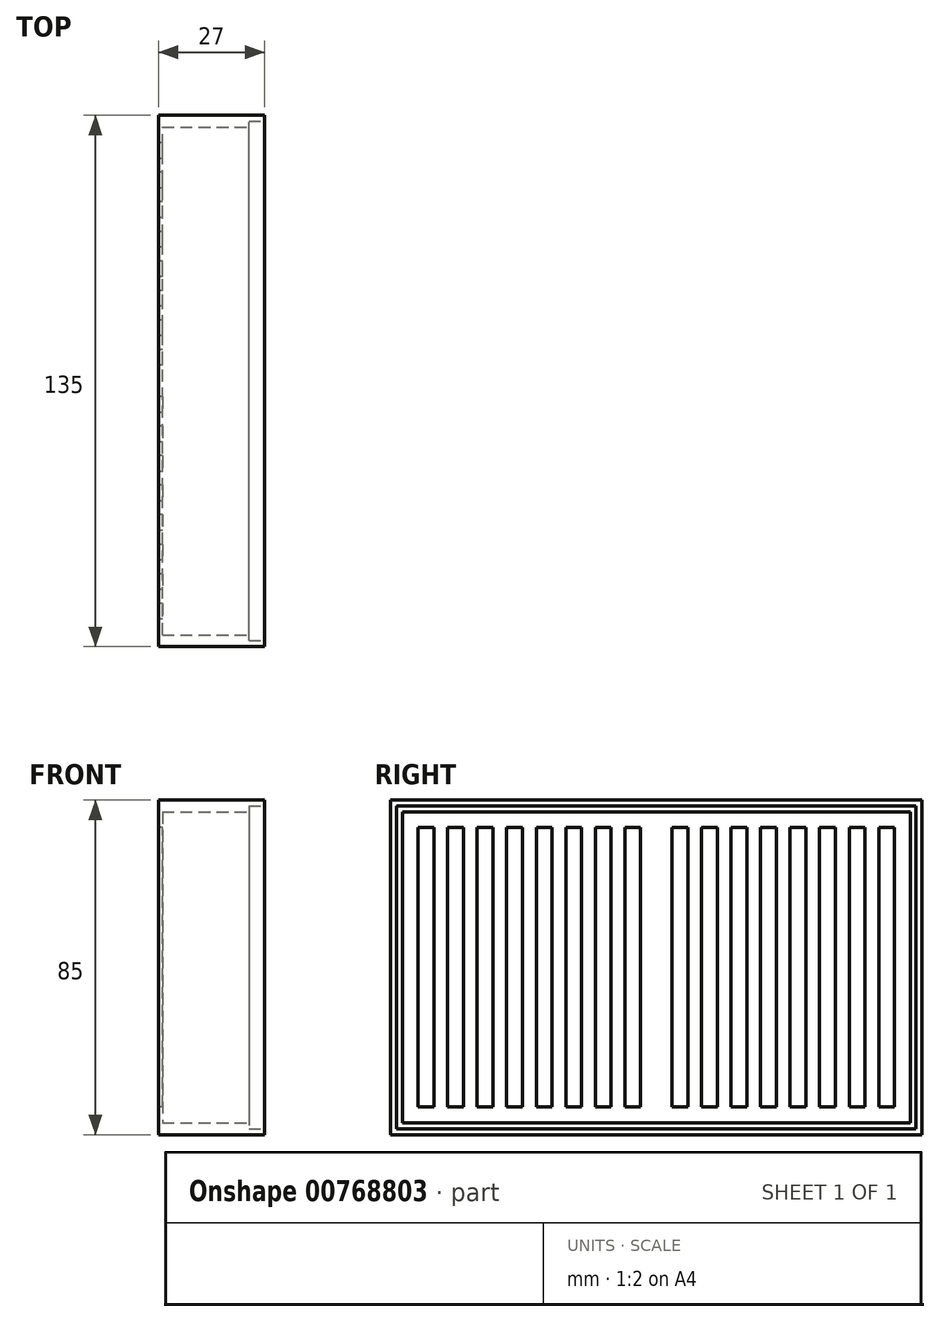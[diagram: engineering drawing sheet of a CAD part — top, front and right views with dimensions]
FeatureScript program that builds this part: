
annotation { "Feature Type Name" : "Feature", "Feature Type Description" : "" }
export const myFeature = defineFeature(function(context is Context, id is Id, definition is map)
    precondition{}
    {
        {
            var Q0;
            Q0=qCreatedBy(makeId("Right.planeOp"),FACE);
            var sketch = newSketch(context, id + "F0", { "sketchPlane" : qUnion([Q0])});
            skLineSegment(sketch, "E0.bottom", {"start": v(-67.5, 42.5) * mm, "end": v(67.5, 42.5) * mm});
            skLineSegment(sketch, "E0.top", {"start": v(-67.5, -42.5) * mm, "end": v(67.5, -42.5) * mm});
            skLineSegment(sketch, "E0.left", {"start": v(-67.5, 42.5) * mm, "end": v(-67.5, -42.5) * mm});
            skLineSegment(sketch, "E0.right", {"start": v(67.5, 42.5) * mm, "end": v(67.5, -42.5) * mm});
            skPoint(sketch, "E1", {"position": v(0, 42.5) * mm});
            skPoint(sketch, "E2", {"position": v(-67.5, 0) * mm});
            skSolve(sketch);
        }
        {
            var Q0;
            Q0 = qSketchRegion(id + "F0", true);
            extrude(context, id + "F1", {"entities" : qUnion([Q0]), "endBound" : BoundingType.SYMMETRIC, "depth" : 28 * mm, "offsetDistance" : 25 * mm});
        }
        {
            var Q0;
            Q0=makeQuery(id+"F1.opExtrude","CAP_FACE",FACE,{"disambiguationData":[OSD([sQuery(id+"F0.wireOp",EDGE,"E0.bottom"),sQuery(id+"F0.wireOp",EDGE,"E0.top"),sQuery(id+"F0.wireOp",EDGE,"E0.left"),sQuery(id+"F0.wireOp",EDGE,"E0.right")])],"isStart":false});
            var sketch = newSketch(context, id + "F2", { "sketchPlane" : qUnion([Q0])});
            skLineSegment(sketch, "E3.bottom", {"start": v(-64.5, 39.5) * mm, "end": v(64.5, 39.5) * mm});
            skLineSegment(sketch, "E3.top", {"start": v(-64.5, -39.5) * mm, "end": v(64.5, -39.5) * mm});
            skLineSegment(sketch, "E3.left", {"start": v(-64.5, 39.5) * mm, "end": v(-64.5, -39.5) * mm});
            skLineSegment(sketch, "E3.right", {"start": v(64.5, 39.5) * mm, "end": v(64.5, -39.5) * mm});
            skSolve(sketch);
        }
        {
            var Q0;
            Q0 = qSketchRegion(id + "F2", true);
            extrude(context, id + "F3", {"entities" : qUnion([Q0]), "operationType" : NewBodyOperationType.REMOVE, "oppositeDirection" : true, "depth" : 26 * mm, "offsetDistance" : 25 * mm});
        }
        {
            var Q0;
            Q0=makeQuery(id+"F1.opExtrude","CAP_FACE",FACE,{"disambiguationData":[OSD([sQuery(id+"F0.wireOp",EDGE,"E0.bottom"),sQuery(id+"F0.wireOp",EDGE,"E0.top"),sQuery(id+"F0.wireOp",EDGE,"E0.left"),sQuery(id+"F0.wireOp",EDGE,"E0.right")])],"isStart":false});
            var sketch = newSketch(context, id + "F4", { "sketchPlane" : qUnion([Q0])});
            skLineSegment(sketch, "E4.bottom", {"start": v(-66, 41) * mm, "end": v(66, 41) * mm});
            skLineSegment(sketch, "E4.top", {"start": v(-66, -41) * mm, "end": v(66, -41) * mm});
            skLineSegment(sketch, "E4.left", {"start": v(-66, 41) * mm, "end": v(-66, -41) * mm});
            skLineSegment(sketch, "E4.right", {"start": v(66, 41) * mm, "end": v(66, -41) * mm});
            skLineSegment(sketch, "E5.bottom", {"start": v(-64.5, 39.5) * mm, "end": v(64.5, 39.5) * mm});
            skLineSegment(sketch, "E5.top", {"start": v(-64.5, -39.5) * mm, "end": v(64.5, -39.5) * mm});
            skLineSegment(sketch, "E5.left", {"start": v(-64.5, 39.5) * mm, "end": v(-64.5, -39.5) * mm});
            skLineSegment(sketch, "E5.right", {"start": v(64.5, 39.5) * mm, "end": v(64.5, -39.5) * mm});
            skSolve(sketch);
        }
        {
            var Q0;
            Q0 = qSketchRegion(id + "F4", true);
            extrude(context, id + "F5", {"entities" : qUnion([Q0]), "operationType" : NewBodyOperationType.REMOVE, "oppositeDirection" : true, "depth" : 3 * mm, "offsetDistance" : 25 * mm});
        }
        {
            var Q0;
            Q0=makeQuery(id+"F1.opExtrude","CAP_FACE",FACE,{"disambiguationData":[OSD([sQuery(id+"F0.wireOp",EDGE,"E0.bottom"),sQuery(id+"F0.wireOp",EDGE,"E0.top"),sQuery(id+"F0.wireOp",EDGE,"E0.left"),sQuery(id+"F0.wireOp",EDGE,"E0.right")])],"isStart":true});
            var sketch = newSketch(context, id + "F6", { "sketchPlane" : qUnion([Q0])});
            skLineSegment(sketch, "E6.bottom", {"start": v(-60.5, 35.5) * mm, "end": v(-56.5, 35.5) * mm});
            skLineSegment(sketch, "E6.top", {"start": v(-60.5, -35.5) * mm, "end": v(-56.5, -35.5) * mm});
            skLineSegment(sketch, "E6.left", {"start": v(-60.5, 35.5) * mm, "end": v(-60.5, -35.5) * mm});
            skLineSegment(sketch, "E6.right", {"start": v(-56.5, 35.5) * mm, "end": v(-56.5, -35.5) * mm});
            skLineSegment(sketch, "E7.1.0.0", {"start": v(-53, 35.5) * mm, "end": v(-53, -35.5) * mm});
            skLineSegment(sketch, "E7.1.0.1", {"start": v(-49, 35.5) * mm, "end": v(-49, -35.5) * mm});
            skLineSegment(sketch, "E7.1.0.2", {"start": v(-53, 35.5) * mm, "end": v(-49, 35.5) * mm});
            skLineSegment(sketch, "E7.1.0.3", {"start": v(-53, -35.5) * mm, "end": v(-49, -35.5) * mm});
            skLineSegment(sketch, "E7.2.0.0", {"start": v(-45.5, 35.5) * mm, "end": v(-45.5, -35.5) * mm});
            skLineSegment(sketch, "E7.2.0.1", {"start": v(-41.5, 35.5) * mm, "end": v(-41.5, -35.5) * mm});
            skLineSegment(sketch, "E7.2.0.2", {"start": v(-45.5, 35.5) * mm, "end": v(-41.5, 35.5) * mm});
            skLineSegment(sketch, "E7.2.0.3", {"start": v(-45.5, -35.5) * mm, "end": v(-41.5, -35.5) * mm});
            skLineSegment(sketch, "E7.3.0.0", {"start": v(-38, 35.5) * mm, "end": v(-38, -35.5) * mm});
            skLineSegment(sketch, "E7.3.0.1", {"start": v(-34, 35.5) * mm, "end": v(-34, -35.5) * mm});
            skLineSegment(sketch, "E7.3.0.2", {"start": v(-38, 35.5) * mm, "end": v(-34, 35.5) * mm});
            skLineSegment(sketch, "E7.3.0.3", {"start": v(-38, -35.5) * mm, "end": v(-34, -35.5) * mm});
            skLineSegment(sketch, "E7.4.0.0", {"start": v(-30.5, 35.5) * mm, "end": v(-30.5, -35.5) * mm});
            skLineSegment(sketch, "E7.4.0.1", {"start": v(-26.5, 35.5) * mm, "end": v(-26.5, -35.5) * mm});
            skLineSegment(sketch, "E7.4.0.2", {"start": v(-30.5, 35.5) * mm, "end": v(-26.5, 35.5) * mm});
            skLineSegment(sketch, "E7.4.0.3", {"start": v(-30.5, -35.5) * mm, "end": v(-26.5, -35.5) * mm});
            skLineSegment(sketch, "E7.5.0.0", {"start": v(-23, 35.5) * mm, "end": v(-23, -35.5) * mm});
            skLineSegment(sketch, "E7.5.0.1", {"start": v(-19, 35.5) * mm, "end": v(-19, -35.5) * mm});
            skLineSegment(sketch, "E7.5.0.2", {"start": v(-23, 35.5) * mm, "end": v(-19, 35.5) * mm});
            skLineSegment(sketch, "E7.5.0.3", {"start": v(-23, -35.5) * mm, "end": v(-19, -35.5) * mm});
            skLineSegment(sketch, "E7.6.0.0", {"start": v(-15.5, 35.5) * mm, "end": v(-15.5, -35.5) * mm});
            skLineSegment(sketch, "E7.6.0.1", {"start": v(-11.5, 35.5) * mm, "end": v(-11.5, -35.5) * mm});
            skLineSegment(sketch, "E7.6.0.2", {"start": v(-15.5, 35.5) * mm, "end": v(-11.5, 35.5) * mm});
            skLineSegment(sketch, "E7.6.0.3", {"start": v(-15.5, -35.5) * mm, "end": v(-11.5, -35.5) * mm});
            skLineSegment(sketch, "E7.7.0.0", {"start": v(-8, 35.5) * mm, "end": v(-8, -35.5) * mm});
            skLineSegment(sketch, "E7.7.0.1", {"start": v(-4, 35.5) * mm, "end": v(-4, -35.5) * mm});
            skLineSegment(sketch, "E7.7.0.2", {"start": v(-8, 35.5) * mm, "end": v(-4, 35.5) * mm});
            skLineSegment(sketch, "E7.7.0.3", {"start": v(-8, -35.5) * mm, "end": v(-4, -35.5) * mm});
            skLineSegment(sketch, "E7.direction1", {"start": v(-60.5, -35.5) * mm, "end": v(-53, -35.5) * mm, "construction": true});
            skLineSegment(sketch, "E8.MirrorCS", {"start": v(60.5, -35.5) * mm, "end": v(53, -35.5) * mm, "construction": true});
            skLineSegment(sketch, "E9.MirrorCS", {"start": v(45.5, 35.5) * mm, "end": v(41.5, 35.5) * mm});
            skLineSegment(sketch, "E10.MirrorCS", {"start": v(45.5, -35.5) * mm, "end": v(41.5, -35.5) * mm});
            skLineSegment(sketch, "E11.MirrorCS", {"start": v(23, -35.5) * mm, "end": v(19, -35.5) * mm});
            skLineSegment(sketch, "E12.MirrorCS", {"start": v(30.5, 35.5) * mm, "end": v(26.5, 35.5) * mm});
            skLineSegment(sketch, "E13.MirrorCS", {"start": v(15.5, 35.5) * mm, "end": v(11.5, 35.5) * mm});
            skLineSegment(sketch, "E14.MirrorCS", {"start": v(30.5, -35.5) * mm, "end": v(26.5, -35.5) * mm});
            skLineSegment(sketch, "E15.MirrorCS", {"start": v(60.5, -35.5) * mm, "end": v(56.5, -35.5) * mm});
            skLineSegment(sketch, "E16.MirrorCS", {"start": v(60.5, 35.5) * mm, "end": v(56.5, 35.5) * mm});
            skLineSegment(sketch, "E17.MirrorCS", {"start": v(38, -35.5) * mm, "end": v(34, -35.5) * mm});
            skLineSegment(sketch, "E18.MirrorCS", {"start": v(38, 35.5) * mm, "end": v(34, 35.5) * mm});
            skLineSegment(sketch, "E19.MirrorCS", {"start": v(53, -35.5) * mm, "end": v(49, -35.5) * mm});
            skLineSegment(sketch, "E20.MirrorCS", {"start": v(23, 35.5) * mm, "end": v(19, 35.5) * mm});
            skLineSegment(sketch, "E21.MirrorCS", {"start": v(8, -35.5) * mm, "end": v(4, -35.5) * mm});
            skLineSegment(sketch, "E22.MirrorCS", {"start": v(53, 35.5) * mm, "end": v(49, 35.5) * mm});
            skLineSegment(sketch, "E23.MirrorCS", {"start": v(8, 35.5) * mm, "end": v(4, 35.5) * mm});
            skLineSegment(sketch, "E24.MirrorCS", {"start": v(15.5, -35.5) * mm, "end": v(11.5, -35.5) * mm});
            skLineSegment(sketch, "E25.MirrorCS", {"start": v(45.5, 35.5) * mm, "end": v(45.5, -35.5) * mm});
            skLineSegment(sketch, "E26.MirrorCS", {"start": v(41.5, 35.5) * mm, "end": v(41.5, -35.5) * mm});
            skLineSegment(sketch, "E27.MirrorCS", {"start": v(30.5, 35.5) * mm, "end": v(30.5, -35.5) * mm});
            skLineSegment(sketch, "E28.MirrorCS", {"start": v(38, 35.5) * mm, "end": v(38, -35.5) * mm});
            skLineSegment(sketch, "E29.MirrorCS", {"start": v(26.5, 35.5) * mm, "end": v(26.5, -35.5) * mm});
            skLineSegment(sketch, "E30.MirrorCS", {"start": v(15.5, 35.5) * mm, "end": v(15.5, -35.5) * mm});
            skLineSegment(sketch, "E31.MirrorCS", {"start": v(11.5, 35.5) * mm, "end": v(11.5, -35.5) * mm});
            skLineSegment(sketch, "E32.MirrorCS", {"start": v(34, 35.5) * mm, "end": v(34, -35.5) * mm});
            skLineSegment(sketch, "E33.MirrorCS", {"start": v(19, 35.5) * mm, "end": v(19, -35.5) * mm});
            skLineSegment(sketch, "E34.MirrorCS", {"start": v(8, 35.5) * mm, "end": v(8, -35.5) * mm});
            skLineSegment(sketch, "E35.MirrorCS", {"start": v(49, 35.5) * mm, "end": v(49, -35.5) * mm});
            skLineSegment(sketch, "E36.MirrorCS", {"start": v(53, 35.5) * mm, "end": v(53, -35.5) * mm});
            skLineSegment(sketch, "E37.MirrorCS", {"start": v(56.5, 35.5) * mm, "end": v(56.5, -35.5) * mm});
            skLineSegment(sketch, "E38.MirrorCS", {"start": v(60.5, 35.5) * mm, "end": v(60.5, -35.5) * mm});
            skLineSegment(sketch, "E39.MirrorCS", {"start": v(4, 35.5) * mm, "end": v(4, -35.5) * mm});
            skLineSegment(sketch, "E40.MirrorCS", {"start": v(23, 35.5) * mm, "end": v(23, -35.5) * mm});
            skSolve(sketch);
        }
        {
            var Q0;
            Q0 = qSketchRegion(id + "F6", true);
            extrude(context, id + "F7", {"entities" : qUnion([Q0]), "operationType" : NewBodyOperationType.REMOVE, "oppositeDirection" : true, "depth" : 25 * mm, "offsetDistance" : 25 * mm});
        }
        {
            var Q0;
            Q0=makeQuery(id+"F1.opExtrude","CAP_FACE",FACE,{"disambiguationData":[OSD([sQuery(id+"F0.wireOp",EDGE,"E0.bottom"),sQuery(id+"F0.wireOp",EDGE,"E0.top"),sQuery(id+"F0.wireOp",EDGE,"E0.left"),sQuery(id+"F0.wireOp",EDGE,"E0.right")])],"isStart":true});
            extrude(context, id + "F8", {"entities" : qUnion([Q0]), "operationType" : NewBodyOperationType.REMOVE, "oppositeDirection" : true, "depth" : 1 * mm, "offsetDistance" : 25 * mm});
        }
        {
            var Q0;
            Q0=makeQuery(id+"F5.boolean.opBoolean","COPY",FACE,{"derivedFrom":makeQuery(id+"F5.opExtrude","CAP_FACE",FACE,{"disambiguationData":[OSD([sQuery(id+"F4.wireOp",EDGE,"E4.bottom"),sQuery(id+"F4.wireOp",EDGE,"E4.top"),sQuery(id+"F4.wireOp",EDGE,"E4.left"),sQuery(id+"F4.wireOp",EDGE,"E4.right"),sQuery(id+"F4.wireOp",EDGE,"E5.bottom"),sQuery(id+"F4.wireOp",EDGE,"E5.top"),sQuery(id+"F4.wireOp",EDGE,"E5.left"),sQuery(id+"F4.wireOp",EDGE,"E5.right")])],"isStart":false})});
            extrude(context, id + "F9", {"entities" : qUnion([Q0]), "operationType" : NewBodyOperationType.REMOVE, "oppositeDirection" : true, "depth" : 1 * mm, "offsetDistance" : 25 * mm});
        }
    });
